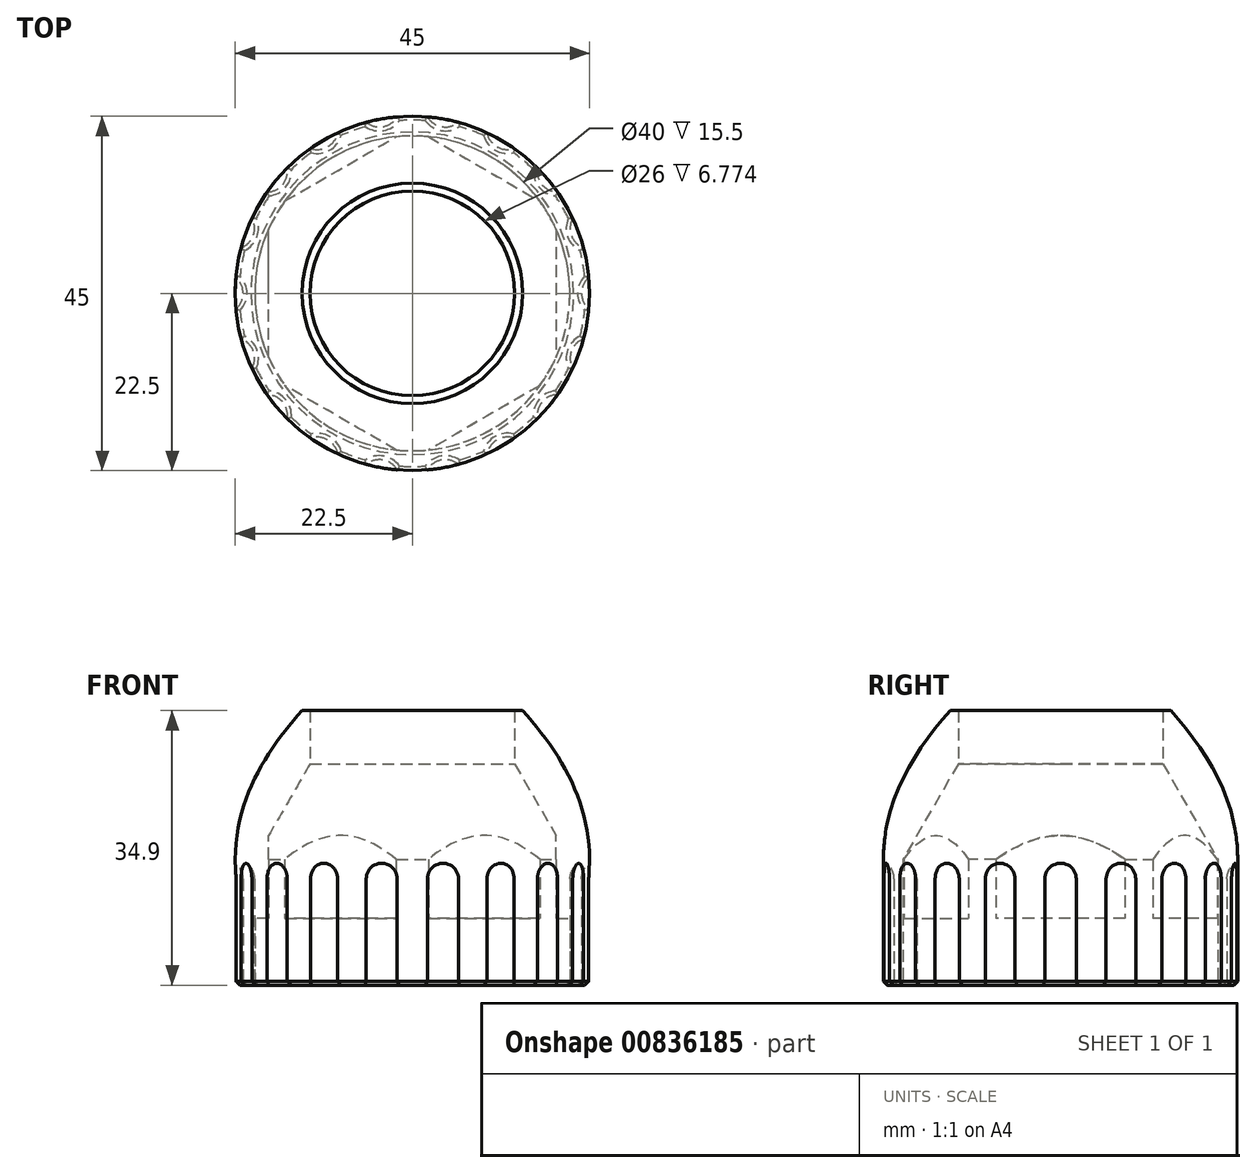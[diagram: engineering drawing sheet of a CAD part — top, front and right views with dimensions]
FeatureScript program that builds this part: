
annotation { "Feature Type Name" : "Feature", "Feature Type Description" : "" }
export const myFeature = defineFeature(function(context is Context, id is Id, definition is map)
    precondition{}
    {
        {
            var Q0;
            Q0=qCreatedBy(makeId("Front.planeOp"),FACE);
            var sketch = newSketch(context, id + "F0", { "sketchPlane" : qUnion([Q0])});
            skLineSegment(sketch, "E0", {"start": v(-22.5, 0) * mm, "end": v(-22.5, 16) * mm});
            skLineSegment(sketch, "E1", {"start": v(-13, 28.12) * mm, "end": v(-13, 36) * mm});
            skLineSegment(sketch, "E2", {"start": v(-20, 0) * mm, "end": v(-20, 16) * mm});
            skLineSegment(sketch, "E3", {"start": v(-20, 16) * mm, "end": v(-13, 28.12) * mm});
            skLineSegment(sketch, "E4", {"start": v(-22.5, 0) * mm, "end": v(-20, 0) * mm});
            skLineSegment(sketch, "E5", {"start": v(-13, 36) * mm, "end": v(-6.58, 36) * mm, "construction": true});
            skLineSegment(sketch, "E6", {"start": v(0, 0) * mm, "end": v(0, 60.14) * mm});
            skLineSegment(sketch, "E7.MirrorCS", {"start": v(22.5, 0) * mm, "end": v(20, 0) * mm});
            skLineSegment(sketch, "E8.MirrorCS", {"start": v(20, 16) * mm, "end": v(13, 28.12) * mm});
            skLineSegment(sketch, "E9.MirrorCS", {"start": v(22.5, 0) * mm, "end": v(22.5, 16) * mm});
            skLineSegment(sketch, "E10.MirrorCS", {"start": v(20, 0) * mm, "end": v(20, 16) * mm});
            skLineSegment(sketch, "E11.MirrorCS", {"start": v(13, 28.12) * mm, "end": v(13, 36) * mm});
            skLineSegment(sketch, "E12", {"start": v(-13, 36) * mm, "end": v(-28.53, 19.2) * mm, "construction": true});
            skFitSpline(sketch, "E13", {"points": [v(-22.5, 16) * mm, v(-13, 36) * mm], "startDerivative": vector(0, 25.88) * mm, "endDerivative": vector(13.6, 14.7) * mm});
            skLineSegment(sketch, "E14", {"start": v(-14, 34.9) * mm, "end": v(-13, 34.9) * mm});
            skSolve(sketch);
        }
        {
            var Q0;
            Q0=makeQuery(id+"F0.imprint","IMPRINT",FACE,{"disambiguationData":[TD([[makeQuery(id+"F0.imprint","IMPRINT",EDGE,{"derivedFrom":sQuery(id+"F0.wireOp",EDGE,"E0")}),-1.0]])]});
            var Q1;
            Q1=sQuery(id+"F0.wireOp",EDGE,"E6");
            revolve(context, id + "F1", {"surfaceOperationType" : NewSurfaceOperationType.NEW, "entities" : qUnion([Q0]), "axis" : qUnion([Q1]), "revolveType" : RevolveType.FULL});
        }
        {
            var Q0;
            Q0=qCreatedBy(makeId("Top.planeOp"),FACE);
            var sketch = newSketch(context, id + "F2", { "sketchPlane" : qUnion([Q0])});
            skCircle(sketch, "E15.cCircle", {"center": v(0, 0) * mm, "radius": 18.25 * mm, "construction": true});
            skLineSegment(sketch, "E15.0", {"start": v(18.25, 10.54) * mm, "end": v(18.25, -10.54) * mm});
            skLineSegment(sketch, "E15.1", {"start": v(18.25, -10.54) * mm, "end": v(0, -21.07) * mm});
            skLineSegment(sketch, "E15.2", {"start": v(0, -21.07) * mm, "end": v(-18.25, -10.54) * mm});
            skLineSegment(sketch, "E15.3", {"start": v(-18.25, -10.54) * mm, "end": v(-18.25, 10.54) * mm});
            skLineSegment(sketch, "E15.4", {"start": v(-18.25, 10.54) * mm, "end": v(0, 21.07) * mm});
            skLineSegment(sketch, "E15.5", {"start": v(0, 21.07) * mm, "end": v(18.25, 10.54) * mm});
            skPoint(sketch, "E15.0.midPoint", {"position": v(18.25, 0) * mm});
            skCircle(sketch, "E16", {"center": v(0, 0) * mm, "radius": 22.5 * mm});
            skSolve(sketch);
        }
        {
            var Q0;
            Q0=makeQuery(id+"F2.imprint","IMPRINT",FACE,{"disambiguationData":[TD([[makeQuery(id+"F2.imprint","IMPRINT",EDGE,{"derivedFrom":sQuery(id+"F2.wireOp",EDGE,"E15.0")}),1.0]])]});
            var Q1;
            Q1=makeQuery(id+"F1.opRevolve","SWEPT_FACE",FACE,{"disambiguationData":[OSD([sQuery(id+"F0.wireOp",EDGE,"E3")])]});
            extrude(context, id + "F3", {"entities" : qUnion([Q0]), "operationType" : NewBodyOperationType.ADD, "endBound" : BoundingType.UP_TO_SURFACE, "depth" : 25 * mm, "endBoundEntityFace" : qUnion([Q1]), "offsetDistance" : 25 * mm, "hasSecondDirection" : true, "secondDirectionOppositeDirection" : false, "secondDirectionDepth" : (16 - 7.5) * mm});
        }
        {
            var Q0;
            Q0=qCreatedBy(makeId("Top.planeOp"),FACE);
            var sketch = newSketch(context, id + "F4", { "sketchPlane" : qUnion([Q0])});
            skCircle(sketch, "E17", {"center": v(0, 0) * mm, "radius": 22.5 * mm, "construction": true});
            skCircle(sketch, "E18", {"center": v(-24.15, 0) * mm, "radius": 2.65 * mm});
            skPoint(sketch, "E19", {"position": v(-22.41, 2) * mm});
            skPoint(sketch, "E20", {"position": v(-22.41, -2) * mm});
            skSolve(sketch);
        }
        {
            var Q0;
            Q0 = qSketchRegion(id + "F4", true);
            extrude(context, id + "F5", {"entities" : qUnion([Q0]), "depth" : 16 * mm, "offsetDistance" : 25 * mm});
        }
        {
            var Q0;
            Q0=makeQuery(id+"F5.opExtrude","CAP_EDGE",EDGE,{"disambiguationData":[OSD([sQuery(id+"F4.wireOp",EDGE,"E18")])],"isStart":false});
            fillet(context, id + "F6", {"entities" : qUnion([Q0]), "radius" : 2.5 * mm, "tangentPropagation" : true, "allowEdgeOverflow" : false});
        }
        {
            var Q0;
            Q0=makeQuery(id+"F5.opExtrude","SWEPT_BODY",BODY,{"disambiguationData":[OSD([sQuery(id+"F4.wireOp",EDGE,"E18")])]});
            var Q1;
            Q1=sQuery(id+"F0.wireOp",EDGE,"E6");
            circularPattern(context, id + "F7", {"operationType" : NewBodyOperationType.REMOVE, "entities" : qUnion([Q0]), "axis" : qUnion([Q1]), "angle" : 360 * degree, "instanceCount" : 18, "equalSpace" : true});
        }
        {
            var Q0;
            Q0=makeQuery(id+"F1.opRevolve","SWEPT_FACE",FACE,{"disambiguationData":[OSD([sQuery(id+"F0.wireOp",EDGE,"E4")])]});
            chamfer(context, id + "F8", {"entities" : qUnion([Q0]), "width" : .5 * mm, "tangentPropagation" : true});
        }
    });
